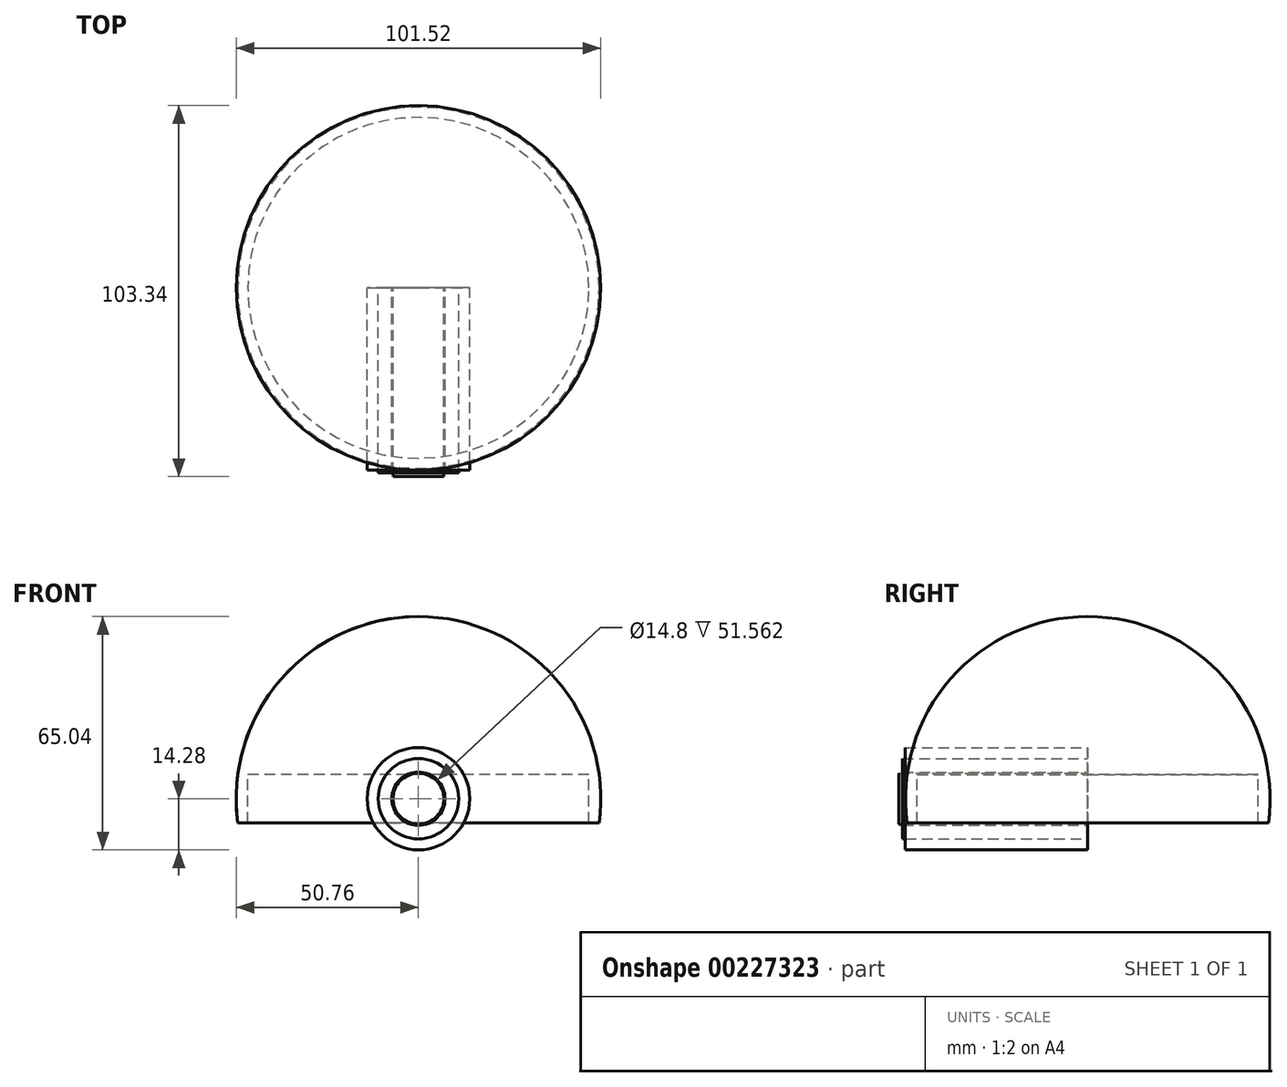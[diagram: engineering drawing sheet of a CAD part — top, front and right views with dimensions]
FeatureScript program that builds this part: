
annotation { "Feature Type Name" : "Feature", "Feature Type Description" : "" }
export const myFeature = defineFeature(function(context is Context, id is Id, definition is map)
    precondition{}
    {
        {
            var Q0;
            Q0=qCreatedBy(makeId("Front.planeOp"),FACE);
            var sketch = newSketch(context, id + "F0", { "sketchPlane" : qUnion([Q0])});
            skCircle(sketch, "E0", {"center": v(0, 0) * mm, "radius": 50.76 * mm});
            skLineSegment(sketch, "E1", {"start": v(-50.32, 6.72) * mm, "end": v(50.32, 6.72) * mm});
            skLineSegment(sketch, "E2.0", {"start": v(-50.31, -6.74) * mm, "end": v(50.31, -6.74) * mm});
            skLineSegment(sketch, "E3", {"start": v(0, 66.33) * mm, "end": v(0, -69.26) * mm});
            skSolve(sketch);
        }
        {
            var Q0;
            {var subQ0=sQuery(id+"F0.wireOp",EDGE,"E1");var subQ1=sQuery(id+"F0.wireOp",EDGE,"E0");var subQ2=makeQuery(id+"F0.imprint","INTERSECT",VERTEX,{"disambiguationData":[OD(0.0)],"derivedFrom":[subQ1,subQ0]});Q0=makeQuery(id+"F0.imprint","IMPRINT",FACE,{"disambiguationData":[TD([[makeQuery(id+"F0.imprint","IMPRINT",EDGE,{"disambiguationData":[TD([[subQ2,1.0]])],"derivedFrom":subQ1}),1.0]])]});}
            var Q1;
            {var subQ0=sQuery(id+"F0.wireOp",EDGE,"E2.0");var subQ1=sQuery(id+"F0.wireOp",EDGE,"E0");var subQ2=makeQuery(id+"F0.imprint","INTERSECT",VERTEX,{"disambiguationData":[OD(1.0)],"derivedFrom":[subQ1,subQ0]});Q1=makeQuery(id+"F0.imprint","IMPRINT",FACE,{"disambiguationData":[TD([[makeQuery(id+"F0.imprint","IMPRINT",EDGE,{"disambiguationData":[TD([[subQ2,1.0]])],"derivedFrom":subQ1}),1.0]])]});}
            var Q2;
            Q2=sQuery(id+"F0.wireOp",EDGE,"E3");
            revolve(context, id + "F1", {"surfaceOperationType" : NewSurfaceOperationType.NEW, "entities" : qUnion([Q0, Q1]), "axis" : qUnion([Q2]), "revolveType" : RevolveType.FULL});
        }
        {
            var Q0;
            Q0=qCreatedBy(makeId("Front.planeOp"),FACE);
            var sketch = newSketch(context, id + "F2", { "sketchPlane" : qUnion([Q0])});
            skLineSegment(sketch, "E4.0", {"start": v(-50.32, 6.72) * mm, "end": v(50.32, 6.72) * mm});
            skLineSegment(sketch, "E5.0", {"start": v(-50.31, -6.74) * mm, "end": v(50.31, -6.74) * mm});
            skLineSegment(sketch, "E6", {"start": v(-47.5, 6.72) * mm, "end": v(-47.5, -6.74) * mm});
            skLineSegment(sketch, "E7", {"start": v(48.3, 6.72) * mm, "end": v(48.3, -6.74) * mm});
            skLineSegment(sketch, "E8", {"start": v(0, 31.26) * mm, "end": v(0, -31.54) * mm});
            skPoint(sketch, "E8.endSnap0", {"position": v(0, -6.74) * mm});
            skSolve(sketch);
        }
        {
            var Q0;
            {var subQ0=sQuery(id+"F2.wireOp",EDGE,"E6");Q0=makeQuery(id+"F2.imprint","IMPRINT",FACE,{"disambiguationData":[TD([[makeQuery(id+"F2.imprint","IMPRINT",EDGE,{"derivedFrom":subQ0}),1.0]])]});}
            var Q1;
            Q1=sQuery(id+"F2.wireOp",EDGE,"E8");
            revolve(context, id + "F3", {"surfaceOperationType" : NewSurfaceOperationType.NEW, "entities" : qUnion([Q0]), "axis" : qUnion([Q1]), "revolveType" : RevolveType.FULL});
        }
        {
            var Q0;
            Q0=qCreatedBy(makeId("Front.planeOp"),FACE);
            var sketch = newSketch(context, id + "F4", { "sketchPlane" : qUnion([Q0])});
            skCircle(sketch, "E9", {"center": v(0, 0) * mm, "radius": 11.19 * mm});
            skCircle(sketch, "E10", {"center": v(0, 0) * mm, "radius": 7.4 * mm});
            skCircle(sketch, "E11", {"center": v(0, 0) * mm, "radius": 4.2 * mm});
            skSolve(sketch);
        }
        {
            var Q0;
            Q0 = qSketchRegion(id + "F4", true);
            extrude(context, id + "F5", {"entities" : qUnion([Q0]), "offsetDistance" : 25.4 * mm, "depth" : 51.56 * mm});
        }
        {
            var Q0;
            Q0=qCreatedBy(makeId("Front.planeOp"),FACE);
            var sketch = newSketch(context, id + "F6", { "sketchPlane" : qUnion([Q0])});
            skCircle(sketch, "E12", {"center": v(0, 0) * mm, "radius": 7.08 * mm});
            skSolve(sketch);
        }
        {
            var Q0;
            Q0 = qSketchRegion(id + "F6", true);
            extrude(context, id + "F7", {"entities" : qUnion([Q0]), "depth" : 52.58 * mm});
        }
        {
            var Q0;
            Q0=qCreatedBy(makeId("Front.planeOp"),FACE);
            var sketch = newSketch(context, id + "F8", { "sketchPlane" : qUnion([Q0])});
            skCircle(sketch, "E13", {"center": v(0, 0) * mm, "radius": 14.28 * mm});
            skSolve(sketch);
        }
        {
            var Q0;
            Q0 = qSketchRegion(id + "F8", true);
            extrude(context, id + "F9", {"entities" : qUnion([Q0]), "depth" : 50.8 * mm});
        }
    });
